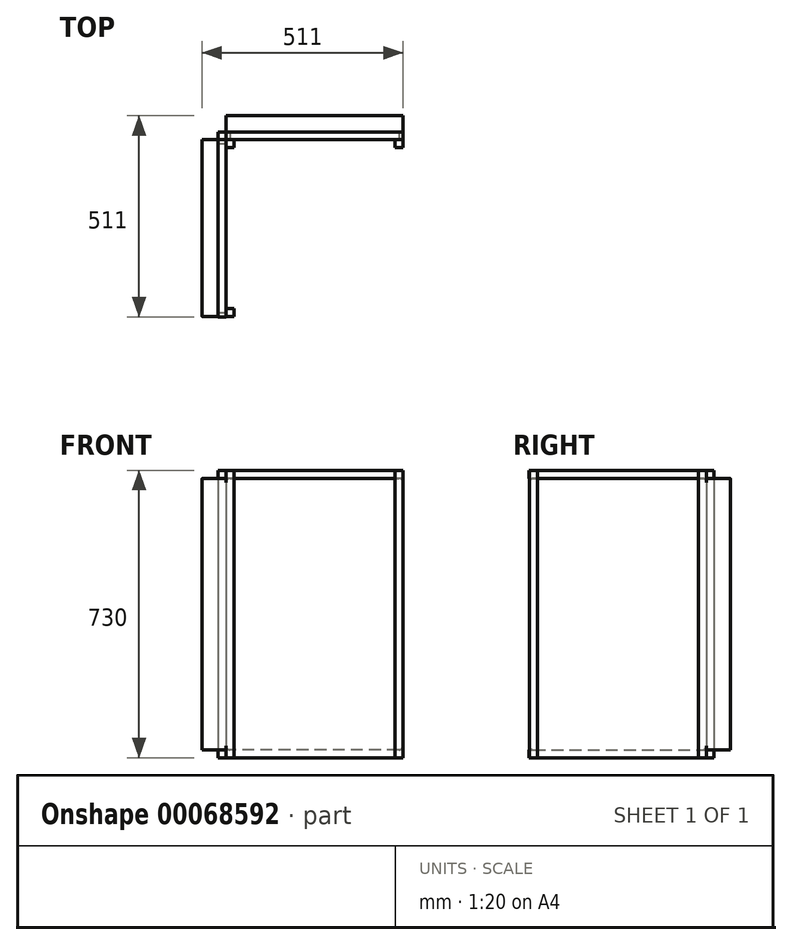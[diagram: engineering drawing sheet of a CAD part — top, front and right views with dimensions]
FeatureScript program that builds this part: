
annotation { "Feature Type Name" : "Feature", "Feature Type Description" : "" }
export const myFeature = defineFeature(function(context is Context, id is Id, definition is map)
    precondition{}
    {
        {
            var Q0;
            Q0=qCreatedBy(makeId("Top.planeOp"),FACE);
            var sketch = newSketch(context, id + "F0", { "sketchPlane" : qUnion([Q0])});
            skLineSegment(sketch, "E0.bottom", {"start": v(0, 0) * mm, "end": v(-20, 0) * mm});
            skLineSegment(sketch, "E0.top", {"start": v(0, 20) * mm, "end": v(-20, 20) * mm});
            skLineSegment(sketch, "E0.left", {"start": v(0, 0) * mm, "end": v(0, 20) * mm});
            skLineSegment(sketch, "E0.right", {"start": v(-20, 0) * mm, "end": v(-20, 20) * mm});
            skLineSegment(sketch, "E1.bottom", {"start": v(0, 0) * mm, "end": v(20, 0) * mm});
            skLineSegment(sketch, "E1.top", {"start": v(0, -20) * mm, "end": v(20, -20) * mm});
            skLineSegment(sketch, "E1.left", {"start": v(0, 0) * mm, "end": v(0, -20) * mm});
            skLineSegment(sketch, "E1.right", {"start": v(20, 0) * mm, "end": v(20, -20) * mm});
            skSolve(sketch);
        }
        {
            assignVariable(context, id + "F1", {"name" : "height", "anyValue" : 730});
        }
        {
            assignVariable(context, id + "F2", {"name" : "width", "anyValue" : 450});
        }
        {
            var Q0;
            Q0=makeQuery(id+"F0.imprint","IMPRINT",FACE,{"disambiguationData":[TD([[makeQuery(id+"F0.imprint","IMPRINT",EDGE,{"derivedFrom":sQuery(id+"F0.wireOp",EDGE,"E0.bottom")}),-1.0]])]});
            extrude(context, id + "F3", {"entities" : qUnion([Q0]), "depth" : (getVariable(context, 'height')) * mm});
        }
        {
            var Q0;
            Q0=makeQuery(id+"F0.imprint","IMPRINT",FACE,{"disambiguationData":[TD([[makeQuery(id+"F0.imprint","IMPRINT",EDGE,{"derivedFrom":sQuery(id+"F0.wireOp",EDGE,"E1.bottom")}),-1.0]])]});
            extrude(context, id + "F4", {"entities" : qUnion([Q0]), "depth" : (getVariable(context, 'height')) * mm});
        }
        {
            var Q0;
            Q0=makeQuery(id+"F3.opExtrude","SWEPT_FACE",FACE,{"disambiguationData":[OSD([sQuery(id+"F0.wireOp",EDGE,"E0.left")])]});
            var sketch = newSketch(context, id + "F5", { "sketchPlane" : qUnion([Q0])});
            skLineSegment(sketch, "E2.bottom", {"start": v(20, 0) * mm, "end": v(0, 0) * mm});
            skLineSegment(sketch, "E2.top", {"start": v(20, 20) * mm, "end": v(0, 20) * mm});
            skLineSegment(sketch, "E2.left", {"start": v(20, 0) * mm, "end": v(20, 20) * mm});
            skLineSegment(sketch, "E2.right", {"start": v(0, 0) * mm, "end": v(0, 20) * mm});
            skSolve(sketch);
        }
        {
            var Q0;
            Q0 = qSketchRegion(id + "F5", true);
            extrude(context, id + "F6", {"entities" : qUnion([Q0]), "depth" : (getVariable(context, 'width')) * mm});
        }
        {
            var Q0;
            Q0=makeQuery(id+"F4.opExtrude","SWEPT_FACE",FACE,{"disambiguationData":[OSD([sQuery(id+"F0.wireOp",EDGE,"E1.bottom")])]});
            var sketch = newSketch(context, id + "F7", { "sketchPlane" : qUnion([Q0])});
            skPoint(sketch, "E3.0", {"position": v(0, 20) * mm});
            skLineSegment(sketch, "E4.bottom", {"start": v(-10, 20) * mm, "end": v(-439.2, 20) * mm});
            skLineSegment(sketch, "E4.top", {"start": v(-10, 709.7) * mm, "end": v(-439.2, 709.7) * mm});
            skLineSegment(sketch, "E4.left", {"start": v(0, 30) * mm, "end": v(0, 699.7) * mm});
            skLineSegment(sketch, "E4.right", {"start": v(-449.2, 30) * mm, "end": v(-449.2, 699.7) * mm});
            skPoint(sketch, "E5.visualSharp", {"position": v(-449.2, 709.7) * mm});
            skArc(sketch, "E5.filletArc", {"start": v(-439.2, 709.7) * mm, "mid": v(-446.27, 706.77) * mm, "end": v(-449.2, 699.7) * mm});
            skPoint(sketch, "E6.visualSharp", {"position": v(0, 709.7) * mm});
            skArc(sketch, "E6.filletArc", {"start": v(0, 699.7) * mm, "mid": v(-2.93, 706.77) * mm, "end": v(-10, 709.7) * mm});
            skArc(sketch, "E7.filletArc", {"start": v(-10, 20) * mm, "mid": v(-2.93, 22.93) * mm, "end": v(0, 30) * mm});
            skPoint(sketch, "E8.visualSharp", {"position": v(-449.2, 20) * mm});
            skArc(sketch, "E8.filletArc", {"start": v(-449.2, 30) * mm, "mid": v(-446.27, 22.93) * mm, "end": v(-439.2, 20) * mm});
            skSolve(sketch);
        }
        {
            var Q0;
            Q0 = qSketchRegion(id + "F7", true);
            extrude(context, id + "F8", {"entities" : qUnion([Q0]), "depth" : 61 * mm});
        }
        {
            var Q0;
            Q0=qCreatedBy(makeId("Top.planeOp"),FACE);
            var sketch = newSketch(context, id + "F9", { "sketchPlane" : qUnion([Q0])});
            skLineSegment(sketch, "E9.bottom", {"start": v(449.2, 0) * mm, "end": v(429.2, 0) * mm});
            skLineSegment(sketch, "E9.top", {"start": v(449.2, -20) * mm, "end": v(429.2, -20) * mm});
            skLineSegment(sketch, "E9.left", {"start": v(449.2, 0) * mm, "end": v(449.2, -20) * mm});
            skLineSegment(sketch, "E9.right", {"start": v(429.2, 0) * mm, "end": v(429.2, -20) * mm});
            skPoint(sketch, "E10.0", {"position": v(449.2, 61) * mm});
            skSolve(sketch);
        }
        {
            var Q0;
            Q0 = qSketchRegion(id + "F9", true);
            extrude(context, id + "F10", {"entities" : qUnion([Q0]), "operationType" : NewBodyOperationType.ADD, "depth" : (getVariable(context, 'height')) * mm});
        }
        {
            var Q0;
            Q0=makeQuery(id+"F3.opExtrude","SWEPT_FACE",FACE,{"disambiguationData":[OSD([sQuery(id+"F0.wireOp",EDGE,"E0.left")])]});
            var sketch = newSketch(context, id + "F11", { "sketchPlane" : qUnion([Q0])});
            skPoint(sketch, "E11.0", {"position": v(0, 730) * mm});
            skLineSegment(sketch, "E12.bottom", {"start": v(0, 730) * mm, "end": v(20, 730) * mm});
            skLineSegment(sketch, "E12.top", {"start": v(0, 710) * mm, "end": v(20, 710) * mm});
            skLineSegment(sketch, "E12.left", {"start": v(0, 730) * mm, "end": v(0, 710) * mm});
            skLineSegment(sketch, "E12.right", {"start": v(20, 730) * mm, "end": v(20, 710) * mm});
            skSolve(sketch);
        }
        {
            var Q0;
            Q0 = qSketchRegion(id + "F11", true);
            extrude(context, id + "F12", {"entities" : qUnion([Q0]), "depth" : (getVariable(context, 'width')) * mm});
        }
        {
            var Q0;
            Q0=qCreatedBy(makeId("Top.planeOp"),FACE);
            var sketch = newSketch(context, id + "F13", { "sketchPlane" : qUnion([Q0])});
            skLineSegment(sketch, "E13", {"start": v(0, 0) * mm, "end": v(96, -96) * mm});
            skSolve(sketch);
        }
        {
            var Q0;
            Q0=sQuery(id+"F13.wireOp",EDGE,"E13");
            cPlane(context, id + "F14", {"entities" : qUnion([Q0]), "cplaneType" : CPlaneType.LINE_ANGLE, "offset" : 150 * mm, "angle" : 90 * degree, "width" : 150 * mm, "height" : 150 * mm});
        }
        {
            var Q0;
            Q0=makeQuery(id+"F12.opExtrude","SWEPT_BODY",BODY,{"disambiguationData":[OSD([sQuery(id+"F11.wireOp",EDGE,"E12.bottom"),sQuery(id+"F11.wireOp",EDGE,"E12.top"),sQuery(id+"F11.wireOp",EDGE,"E12.left"),sQuery(id+"F11.wireOp",EDGE,"E12.right")])]});
            var Q1;
            Q1=makeQuery(id+"F6.opExtrude","SWEPT_BODY",BODY,{"disambiguationData":[OSD([sQuery(id+"F5.wireOp",EDGE,"E2.bottom"),sQuery(id+"F5.wireOp",EDGE,"E2.top"),sQuery(id+"F5.wireOp",EDGE,"E2.left"),sQuery(id+"F5.wireOp",EDGE,"E2.right")])]});
            var Q2;
            Q2=makeQuery(id+"F8.opExtrude","SWEPT_BODY",BODY,{"disambiguationData":[OSD([sQuery(id+"F7.wireOp",EDGE,"E4.bottom"),sQuery(id+"F7.wireOp",EDGE,"E4.top"),sQuery(id+"F7.wireOp",EDGE,"E4.left"),sQuery(id+"F7.wireOp",EDGE,"E4.right"),sQuery(id+"F7.wireOp",EDGE,"E5.filletArc"),sQuery(id+"F7.wireOp",EDGE,"E6.filletArc"),sQuery(id+"F7.wireOp",EDGE,"E7.filletArc"),sQuery(id+"F7.wireOp",EDGE,"E8.filletArc")])]});
            var Q3;
            Q3=qCreatedBy(id+"F14.planeOp",FACE);
            mirror(context, id + "F15", {"entities" : qUnion([Q0, Q1, Q2]), "mirrorPlane" : qUnion([Q3])});
        }
    });
